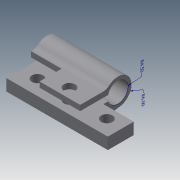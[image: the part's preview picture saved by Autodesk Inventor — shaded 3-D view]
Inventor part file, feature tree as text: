
AUTODESK INVENTOR PART (.ipt)
format: ipt  version: 2019 (Build 230136000, 136)  size: 520,704 bytes
history: native  units: mm
features: extrude x29, sketch x27, other x16, projected_geometry x11, plane x9, direct_edit x8, move_body x4, fillet x3, reference x3, split x2, boolean_combine x1
ambient origin geometry x8: Origin, YZ Plane, XZ Plane, XY Plane, X Axis, Y Axis, Z Axis, Center Point
bodies: Solid1 (feature_tree), Solid2 (feature_tree), Solid3 (feature_tree), Solid4 (feature_tree), Solid5 (feature_tree)
feature tree (113):
  other  "Annotations"
  extrude  "Extrusion1"  Depth=45.0mm
  extrude  "Extrusion4"  Depth=5.0mm
  fillet  "Fillet1"  Radius=11.0mm
  extrude  "Extrusion5"  Depth=23.0mm
  plane  "Work Plane1"
  extrude  "Extrusion6"  Depth=10.0mm
  direct_edit  "Direct Edit1"
  extrude  "Extrusion7"  Depth=12.0mm
  fillet  "Fillet2"  Radius=5.0mm
  plane  "Work Plane5"
  extrude  "Extrusion8"  Depth=5.0mm
  plane  "Work Plane6"
  extrude  "Extrusion9"  Depth=17.8mm
  sketch  "Sketch12"  dims[d34=5.0mm d35=17.8mm]
  extrude  "Extrusion12"  Depth=8.0mm
  extrude  "Extrusion13"  Depth=30.8mm
  extrude  "Extrusion15"  Depth=3.0mm TaperAngle=0.0deg
  plane  "Work Plane7"
  extrude  "Extrusion16"  TaperAngle=0.0deg  [1 undecoded]
  extrude  "Extrusion17"  Depth=18.0mm
  plane  "Work Plane8"
  plane  "Work Plane9"
  split  "Split1"
  split  "Split2"
  boolean_combine  "Combine1"
  direct_edit  "Direct Edit2"
  extrude  "Extrusion18"  Depth=2.0mm
  extrude  "Extrusion20"  Depth=0.5mm TaperAngle=0.0deg
  extrude  "Extrusion21"  Depth=7.25mm TaperAngle=0.0deg
  extrude  "Extrusion22"  Depth=7.25mm TaperAngle=0.0deg
  extrude  "Extrusion23"  Depth=10.0mm TaperAngle=0.0deg
  extrude  "Extrusion24"  Depth=10.0mm
  direct_edit  "Direct Edit3"
  extrude  "Extrusion25"  [1 undecoded]
  sketch  "Sketch24"  dims[d80=10.0mm d81=0.0mm d82=15.0mm]
  plane  "Work Plane10"
  extrude  "Extrusion26"  Depth=3.15mm TaperAngle=0.0deg
  sketch  "Sketch25"  dims[d83=3.0mm d88=-6.0mm]
  plane  "Work Plane11"
  extrude  "Extrusion27"  TaperAngle=0.0deg  [1 undecoded]
  sketch  "Sketch26"  dims[d89=7.5mm d90=3.15mm d91=0.0mm]
  extrude  "Extrusion28"  TaperAngle=0.0deg  [1 undecoded]
  extrude  "Extrusion29"  TaperAngle=0.0deg  [1 undecoded]
  direct_edit  "Direct Edit4"
  sketch  "Sketch28"  dims[d95=0.0mm d96=0.0mm d97=0.0mm d98=-0.3mm]
  plane  "Work Plane12"
  extrude  "Extrusion30"  Depth=10.0mm TaperAngle=0.0deg
  direct_edit  "Direct Edit5"
  extrude  "Extrusion31"  Depth=1.45mm TaperAngle=0.0deg
  extrude  "Extrusion32"  Depth=0.105mm TaperAngle=0.0deg
  direct_edit  "Direct Edit6"
  direct_edit  "Direct Edit7"
  direct_edit  "Direct Edit8"
  extrude  "Extrusion33"  Depth=4.5mm TaperAngle=0.0deg
  extrude  "Extrusion34"  Depth=4.5mm TaperAngle=0.0deg
  fillet  "Fillet6"  Radius=0.105mm
  extrude  "Extrusion35"  TaperAngle=0.0deg  [1 undecoded]
  sketch  "Sketch1"  dims[d0=6.0mm d1=0.0mm d4=45.0mm]
  sketch  "Sketch5"  dims[d5=5.0mm d6=5.0mm d7=11.0mm]
  sketch  "Sketch6"  dims[d8=11.0mm d9=23.0mm]
  sketch  "Sketch7"  dims[d10=10.0mm d20=13.0mm]
  sketch  "Sketch8"  dims[d24=3.0mm d25=0.0mm d26=12.0mm d27=5.0mm]
  sketch  "Sketch10"  dims[d28=3.0mm d29=0.0mm d33=5.0mm]
  projected_geometry  "Projected Loop2"
  sketch  "Sketch13"  dims[d36=8.0mm d37=17.8mm]
  sketch  "Sketch14"  dims[d38=7.1mm d39=30.8mm]
  sketch  "Sketch15"  dims[d40=7.1mm d41=3.0mm d42=0.0mm]
  sketch  "Sketch17"  dims[d46=0.0mm d47=0.0mm d48=-2.5mm d49=0.0mm d50=0.0mm d51=-2.5mm]
  sketch  "Sketch18"  dims[d52=18.0mm d53=11.0mm]
  sketch  "Sketch19"  dims[d54=2.0mm d55=0.0mm d56=2.0mm]
  projected_geometry  "Projected Loop5"
  sketch  "Sketch20"  dims[d57=0.0mm d58=0.5mm d59=0.0mm]
  projected_geometry  "Projected Loop6"
  sketch  "Sketch21"  dims[d60=0.0mm d61=7.25mm d62=0.0mm]
  projected_geometry  "Projected Loop7"
  sketch  "Sketch22"  dims[d68=5.0mm d69=7.25mm d70=0.0mm]
  projected_geometry  "Projected Loop8"
  sketch  "Sketch23"  dims[d72=2.0mm d73=10.0mm d74=0.0mm]
  reference  "Reference1"
  projected_geometry  "Projected Loop9"
  reference  "Reference3"
  reference  "Reference4"
  sketch  "Sketch27"  dims[d92=2.0mm d93=0.0mm d94=0.0mm]
  projected_geometry  "Projected Loop10"
  sketch  "Sketch29"  dims[d99=0.3mm d100=0.0mm]
  projected_geometry  "Projected Loop11"
  sketch  "Sketch30"  dims[d101=10.0mm d102=0.0mm d105=10.0mm d106=0.0mm]
  projected_geometry  "Projected Loop12"
  sketch  "Sketch32"  dims[d110=1.45mm d111=0.0mm d112=1.45mm d113=0.0mm]
  sketch  "Sketch33"  dims[d114=1.65mm d115=0.0mm d116=0.105mm d117=0.0mm]
  projected_geometry  "Projected Loop13"
  sketch  "Sketch34"  dims[d118=-0.105mm d119=0.105mm d120=0.0mm d121=0.105mm d122=0.0mm d123=0.105mm d124=0.0mm d125=0.0mm d126=0.0mm d127=0.105mm d128=0.0mm d129=-2.0mm d130=10.0mm d131=0.0mm d132=0.0mm d133=0.0mm d134=1.76mm d135=1.0mm d136=0.0mm d137=1.0mm d138=0.0mm d140=-0.5mm d143=1.0mm d144=-1.0mm d145=3.4mm d146=1.0mm d147=-1.0mm d148=10.0mm d149=0.0mm d150=10.0mm d151=0.0mm d152=4.0mm d153=10.0mm d154=0.0mm d84=49.911908mm d85=6.0mm d86=52.109261mm d87=4.5mm]
  projected_geometry  "Projected Loop14"
  other  "Composite1"
  move_body  "Move1"
  move_body  "Move2"
  move_body  "Move3"
  other  "Size1"
  other  "Srf1"
  parser-record x1  (decoder bookkeeping rows leaked as tree rows — omitted from the tree; the rows remain in map.json)
  other  "Cerniera versione 3.iam"
  other  "Cerniera 5.5:1"
  other  "Size2"
  move_body  "Move4"
  other  "Size3"
  other  "Size4"
  other  "Size5"
  other  "Size6"
  other  "Size7"
  other  "Size8"
  other  "Radial Dimension 1"
  other  "Radial Dimension 2"
note: 6 required parameter values undecoded (feature->parameter linkage not recoverable at this tier; creation-order binding heuristic only, values carry confidence <= 0.55)
note: 1 file-system path scrubbed to <path> (originals preserved in map.json)
